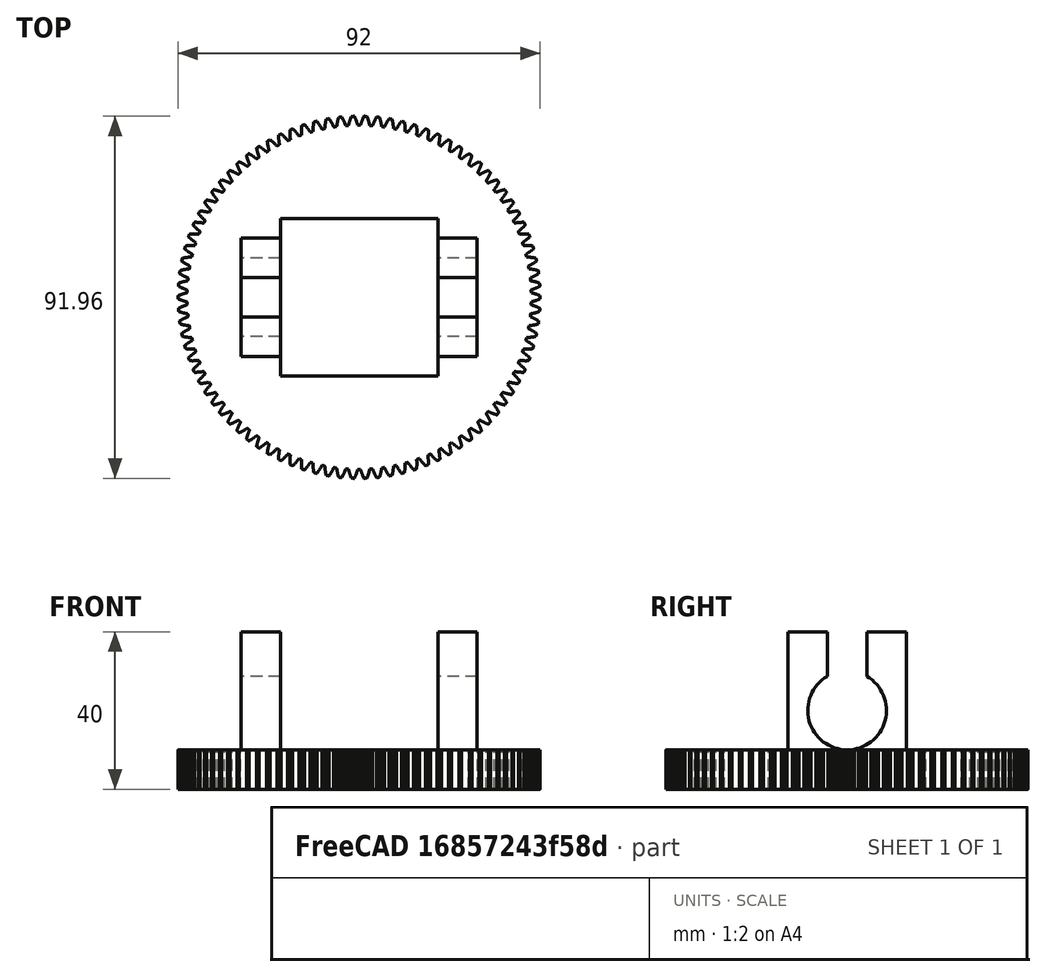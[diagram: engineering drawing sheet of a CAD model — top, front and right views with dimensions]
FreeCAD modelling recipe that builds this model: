
FCSTD DOCUMENT  (FreeCAD 0.17R13522 (Git))
Label: kneecogwheel
License: All rights reserved
LicenseURL: http://en.wikipedia.org/wiki/All_rights_reserved
objects: Part::Box×4, Part::MultiFuse×2, Part::FeaturePython×1, Part::Cylinder×1, Part::Cut×1
note: 9 computed .brp shape members not serialized (recipe doc carries the construction recipe); baked Part::Feature solids carry a one-line shape summary decoded from their .brp

FEATURE [Part::FeaturePython] InvoluteGear  # WARN: FeaturePython — macro-defined, semantics opaque (R4)
  backlash = 0
  beta = 0
  clearance = 0.25
  double_helix = false
  head = 0
  height = 10
  module = 1
  numpoints = 6
  pressure_angle = 20
  reversed_backlash = false
  shift = 0
  simple = false
  teeth = 90
  undercut = false
FEATURE [Part::Box] Box  label="Cube"
  AttacherType = Attacher::AttachEngine3D
  Height = 10
  Length = 40
  Placement = pos=(-20,-20,0) rot=(0,0,1;0rad)
  Width = 40
FEATURE [Part::Box] Box001  label="Cube001"
  AttacherType = Attacher::AttachEngine3D
  Height = 30
  Length = 10
  Placement = pos=(-30,-15,10) rot=(0,0,1;0rad)
  Width = 30
FEATURE [Part::Box] Box002  label="Cube002"
  AttacherType = Attacher::AttachEngine3D
  Height = 30
  Length = 10
  Placement = pos=(20,-15,10) rot=(0,0,1;0rad)
  Width = 30
FEATURE [Part::Cylinder] Cylinder
  Angle = 360
  AttacherType = Attacher::AttachEngine3D
  Height = 80
  Placement = pos=(40,0,20) rot=(0,-1,0;1.5708rad)
  Radius = 10
FEATURE [Part::Box] Box003  label="Cube003"
  AttacherType = Attacher::AttachEngine3D
  Height = 15
  Length = 80
  Placement = pos=(-40,-5,25) rot=(0,0,1;0rad)
  Width = 10
FEATURE [Part::MultiFuse] Fusion  label="Negative Fusion"
  Shapes = -> [Box,Cylinder,Box003]
FEATURE [Part::MultiFuse] Fusion001  label="Positive Fusion"
  Shapes = -> [Box002,Box001,InvoluteGear]
FEATURE [Part::Cut] Cut
  Base = -> Fusion001
  Tool = -> Fusion
